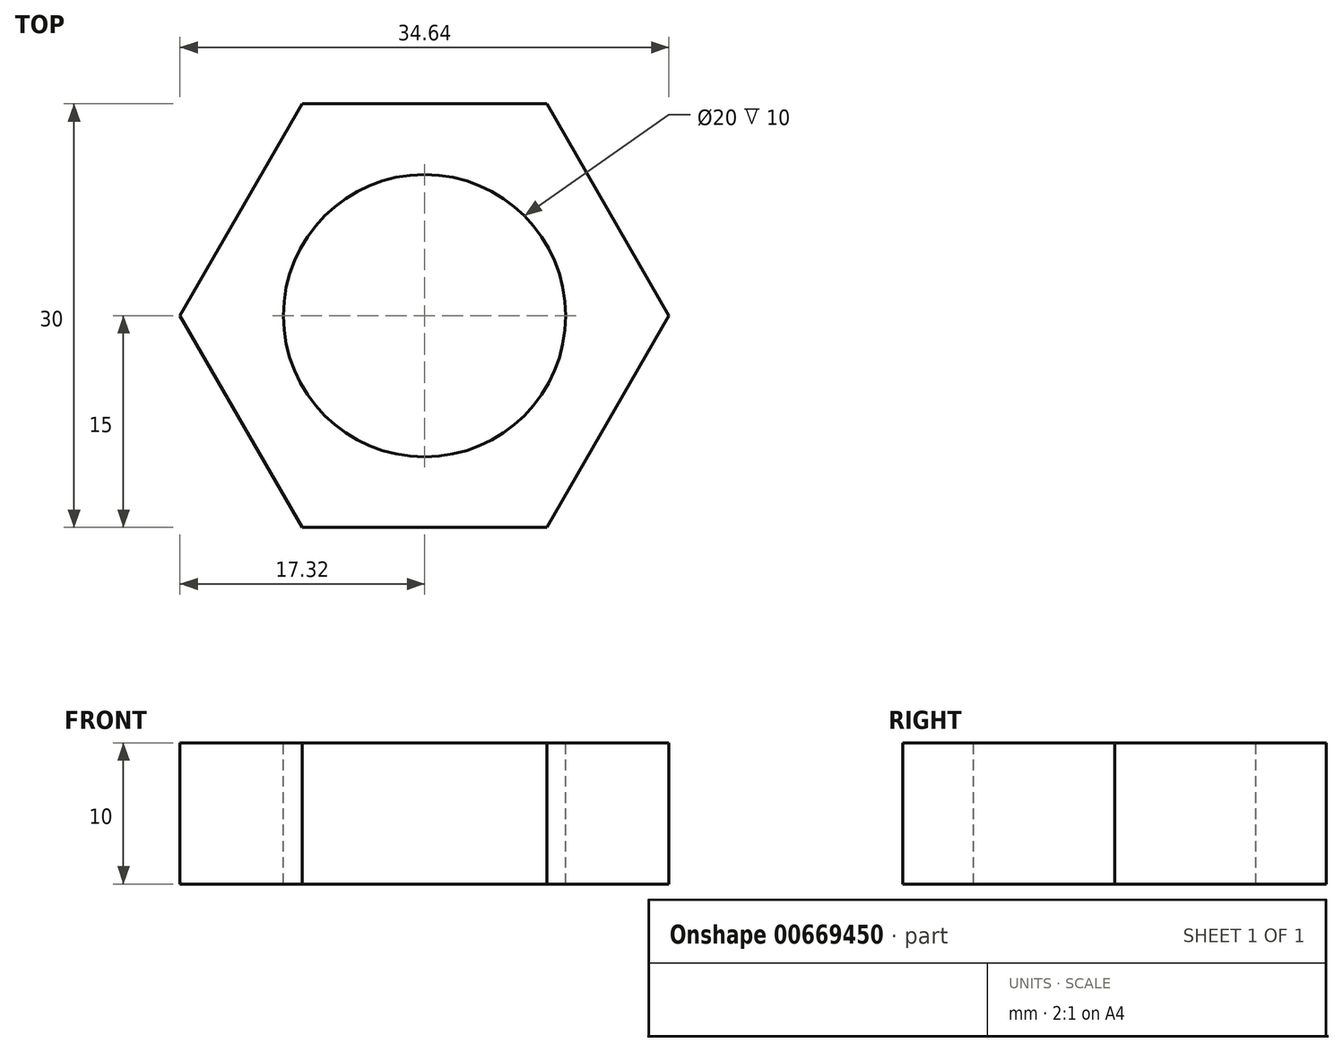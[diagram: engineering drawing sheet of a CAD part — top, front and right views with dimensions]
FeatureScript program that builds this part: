
annotation { "Feature Type Name" : "Feature", "Feature Type Description" : "" }
export const myFeature = defineFeature(function(context is Context, id is Id, definition is map)
    precondition{}
    {
        {
            var Q0;
            Q0=qCreatedBy(makeId("Top.planeOp"),FACE);
            var sketch = newSketch(context, id + "F0", { "sketchPlane" : qUnion([Q0])});
            skCircle(sketch, "E0", {"center": v(-28.35, 27.6) * mm, "radius": 10 * mm});
            skCircle(sketch, "E1.cCircle", {"center": v(-28.35, 27.6) * mm, "radius": 15 * mm, "construction": true});
            skLineSegment(sketch, "E1.0", {"start": v(-19.69, 12.6) * mm, "end": v(-37.01, 12.6) * mm});
            skLineSegment(sketch, "E1.1", {"start": v(-37.01, 12.6) * mm, "end": v(-45.67, 27.6) * mm});
            skLineSegment(sketch, "E1.2", {"start": v(-45.67, 27.6) * mm, "end": v(-37.01, 42.6) * mm});
            skLineSegment(sketch, "E1.3", {"start": v(-37.01, 42.6) * mm, "end": v(-19.69, 42.6) * mm});
            skLineSegment(sketch, "E1.4", {"start": v(-19.69, 42.6) * mm, "end": v(-11.03, 27.6) * mm});
            skLineSegment(sketch, "E1.5", {"start": v(-11.03, 27.6) * mm, "end": v(-19.69, 12.6) * mm});
            skPoint(sketch, "E1.0.midPoint", {"position": v(-28.35, 12.6) * mm});
            skSolve(sketch);
        }
        {
            var Q0;
            Q0=makeQuery(id+"F0.imprint","IMPRINT",FACE,{"disambiguationData":[TD([[makeQuery(id+"F0.imprint","IMPRINT",EDGE,{"derivedFrom":sQuery(id+"F0.wireOp",EDGE,"E0")}),-1.0]])]});
            extrude(context, id + "F1", {"entities" : qUnion([Q0]), "oppositeDirection" : true, "depth" : 10 * mm, "offsetDistance" : 25 * mm});
        }
    });
